# Revit family: Landscaping_Bike-Racks-Shelters_Saris-Infrastructure_Cargo-Bike-Dock
name_source: partatom
category: Site
units: mm (PartAtom-declared; Revit-internal decimal feet)

## family parameters
Always vertical = Yes
Cut with Voids When Loaded = No
OmniClass Number = 23.40.10.11.11
OmniClass Title = Bicycle Racks
Part Type = Normal
Round Connector Dimension = Use Diameter
Shared = No
Work Plane-Based = No

## types (1)
- Cargo Bike Dock
    Default Elevation = 0.00 in
    Description = • 2”x2”x 3/16” structural square tube – square tubing resists efforts from thieves using pipe cutters • Locking bracket hinges into multiple positions depending on bike’s offset to enable use of standard “U” or cable lock • Accommodates two bikes • Low height profile discourages use of standard bikes to reserve spaces for cargo bikes
    Height = 18.25 in
    Length = 35.75 in
    Manufacturer = Saris Infrastructure
    Model = 28385
    Product Documentation Link = https://www.sarisinfrastructure.com
    Product Material = Saris Infrastructure - Mild Steel - Galvanized
    Product Page URL = https://www.sarisinfrastructure.com
    Product Specifications = • 2”x2”x3/16” structural square tube – square tubing resists
efforts from thieves using pipe cuttersrs
• Locking bracket hinges into multiple positions depending on
bike’s offset to enable use of standard “U” or cable lock
• Accommodates two bikes
• Low height profile discourages use of standard bikes to reserve
spaces for cargo bikes
    Type of Mount = Flange
    URL = https://www.sarisinfrastructure.com
    Version = 1
    Warranty = 1 year
    Weight = 46.00 lb
    Width = 5.25 in

## geometry (parser evidence)
native form markers: Extrusion x1, Sweep x5
no freeform markers — native parametric forms only
